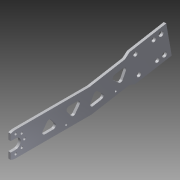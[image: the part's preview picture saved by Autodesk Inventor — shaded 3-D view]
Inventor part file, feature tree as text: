
AUTODESK INVENTOR PART (.ipt)
format: ipt  version: 2013 (Build 170138000, 138)  size: 2,853,376 bytes
history: native  units: mm
features: sketch x6, hole x5, extrude x3, other x2, pattern_circular x1, fillet x1
ambient origin geometry x8: Origin, YZ Plane, XZ Plane, XY Plane, X Axis, Y Axis, Z Axis, Center Point
feature tree (18):
  other  "ソリッド1"
  extrude  "押し出し1"  Depth=20.0mm
  hole  "穴2"  [1 undecoded]
  extrude  "押し出し2"  Depth=10.0mm
  hole  "穴3"  [1 undecoded]
  hole  "穴4"  [1 undecoded]
  pattern_circular  "円形状パターン3"  [2 undecoded]
  hole  "穴5"  [1 undecoded]
  hole  "穴6"  [1 undecoded]
  extrude  "押し出し5"  Depth=4.0mm
  fillet  "フィレット2"  Radius=120.0mm
  sketch  "スケッチ4"
  sketch  "スケッチ6"
  sketch  "スケッチ7"
  sketch  "スケッチ8"
  sketch  "スケッチ11"
  sketch  "スケッチ13"
  other  "断面エッジを投影1"
note: 7 required parameter values undecoded (feature->parameter linkage not recoverable at this tier; creation-order binding heuristic only, values carry confidence <= 0.55)
